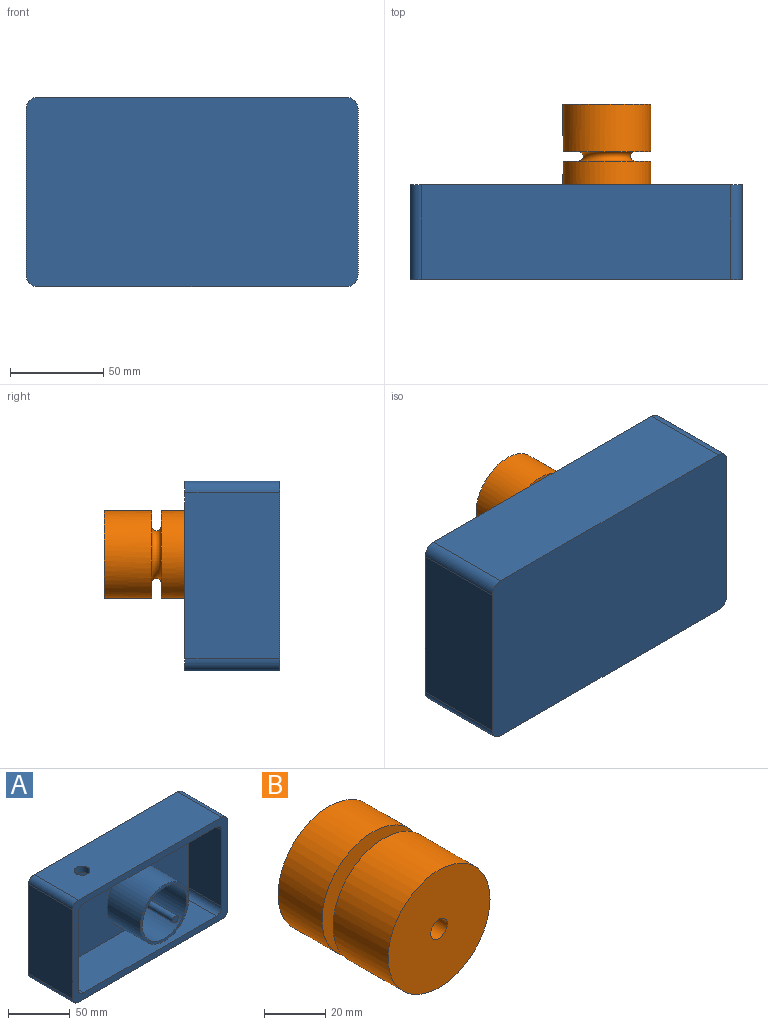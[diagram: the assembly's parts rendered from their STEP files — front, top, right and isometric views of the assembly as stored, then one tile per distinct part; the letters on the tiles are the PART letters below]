
ASSEMBLY  parts=2 mates=1
PART A: 26 faces, bbox 177.8x63.5x101.6 mm
  f0: plane 165.1x50.8mm, normal (0,0,1), area 8260.4mm2, adj f1,f15,f16,f17,f23
  f1: cylinder r=6.35mm len=50.8mm, axis (0,1,0), area 506.7mm2, adj f0,f2,f16,f17
  f2: plane 88.9x50.8mm, normal (-1,0,0), area 4516.1mm2, adj f1,f3,f16,f17
  f3: cylinder r=6.35mm len=50.8mm, axis (0,1,0), area 506.7mm2, adj f2,f4,f16,f17
  f4: plane 165.1x50.8mm, normal (0,0,-1), area 8387.1mm2, adj f3,f5,f16,f17
  f5: cylinder r=6.35mm len=50.8mm, axis (0,1,0), area 506.7mm2, adj f4,f6,f16,f17
  f6: plane 88.9x50.8mm, normal (1,0,0), area 4516.1mm2, adj f5,f15,f16,f17
  f7: cylinder r=6.35mm len=38.1mm, axis (0,1,0), area 380mm2, adj f8,f14,f16,f18
  f8: plane 76.2x38.1mm, normal (1,0,0), area 2903.2mm2, adj f7,f9,f16,f18
  f9: cylinder r=6.35mm len=38.1mm, axis (0,1,0), area 380mm2, adj f8,f10,f16,f18
  f10: plane 152.4x38.1mm, normal (0,0,-1), area 5679.8mm2, adj f9,f11,f16,f18,f23
  f11: cylinder r=6.35mm len=38.1mm, axis (0,1,0), area 380mm2, adj f10,f12,f16,f18
  f12: plane 76.2x38.1mm, normal (-1,0,0), area 2903.2mm2, adj f11,f13,f16,f18
  f13: cylinder r=6.35mm len=38.1mm, axis (0,1,0), area 380mm2, adj f12,f14,f16,f18
  f14: plane 152.4x38.1mm, normal (0,0,1), area 5806.4mm2, adj f7,f13,f16,f18
  f15: cylinder r=6.35mm len=50.8mm, axis (0,1,0), area 506.7mm2, adj f0,f6,f16,f17
  f16: plane 177.8x101.6mm, normal (0,-1,0), area 3387.1mm2, adj f0,f1,f2,f3,f4,f5,f6,f7
  f17: plane 177.8x101.6mm, normal (0,1,0), area 18029.9mm2, adj f0,f1,f2,f3,f4,f5,f6,f15
  f18: plane 165.1x88.9mm, normal (0,-1,0), area 12190.3mm2, adj f7,f8,f9,f10,f11,f12,f13,f14
  f19: plane 55.88x55.88mm, normal (0,-1,0), area 425.6mm2, adj f20,f21
  f20: cylinder r=27.94mm len=55.88mm, axis (0,1,0), area 6688.5mm2, adj f18,f19
  f21: cylinder r=25.4mm len=50.8mm, axis (0,1,0), area 6080.5mm2, adj f19,f22
  f22: plane 50.8x50.8mm, normal (0,-1,0), area 1995.2mm2, adj f21,f24
  f23: cylinder r=6.35mm len=12.7mm, axis (0,0,1), area 253.4mm2, adj f0,f10
  f24: cylinder r=3.17mm len=50.8mm, axis (0,1,0), area 1013.4mm2, adj f22,f25
  f25: plane 6.35x6.35mm, normal (0,-1,0), area 31.7mm2, adj f24
PART B: 8 faces, bbox 47x50.8x47 mm
  f0: cylinder r=23.49mm len=46.99mm, axis (0,1,0), area 3749.6mm2, adj f3,f5
  f1: cylinder r=3.81mm len=50.8mm, axis (0,1,0), area 1216.1mm2, adj f3,f4
  f2: cylinder r=23.49mm len=46.99mm, axis (0,1,0), area 2999.7mm2, adj f4,f6
  f3: plane 46.99x46.99mm, normal (0,-1,0), area 1688.6mm2, adj f0,f1
  f4: plane 46.99x46.99mm, normal (0,1,0), area 1688.6mm2, adj f1,f2
  f5: plane 46.99x46.99mm, normal (0,1,0), area 1015mm2, adj f0,f7
  f6: plane 46.99x46.99mm, normal (0,-1,0), area 1015mm2, adj f2,f7
  f7: torus R=15.13mm, axis (0,-1,0), area 677.5mm2, adj f5,f6
PLACE A rot(axis=(1,0,0),180deg) t=(-16.51,-12.7,-11.43)mm
PLACE B rot(axis=(0.4,0,0.92),180deg) t=(0,30.48,0)mm
MATE cylindrical A.f20 <-> B.f0  axis (0,1,0) through (0,50.8,0)mm
